# Revit family: Furniture-Workstation-Midmark-Care_Exchange-6281-Wall1
name_source: partatom
category: Furniture
revit_build: Autodesk Revit 2016 (Build: 20170117_1200(x64)
units: mm (PartAtom-declared; Revit-internal decimal feet)

## family parameters
Cut with Voids When Loaded = No
Host = Face
OmniClass Number = 23.40.70.11.14.11
OmniClass Title = Medical Equipment
Room Calculation Point = No
Shared = No

## types (2) — shared parameters
Assembly Code = E1020810
Default Elevation = 4' - 0"
Description = Laptop Wall Mounted Workstation
Manufacturer = Midmark
Material = Paint-Midmark-Mist
Model = 6281
Product Documentation Link = http://my.midmark.com
Product Name = MIDMARK 6281-CARE EXCHANGE® WORKSTATION
Product Page URL = http://www.midmark.com
Type Comments = This wall mounted workstation is designed with independent height adjustment for laptop and tablet based technology components.
URL = www.midmark.com

## per-type parameters (varying)
| type | Platform Depth From Wall | Platform Height From Center | Platform Width From Center | Show Extension Arm | Show Standard Arm |
| 6281 | 2' - 0 1/4" | 0' - 11 1/16" | 0' - 0" | No | Yes |
| 6281 - Extension Arm | 2' - 8" | 0' - 7 1/16" | 0' - 1 1/8" | Yes | No |

## geometry (parser evidence)
native form markers: Blend x2, Sweep x19
no freeform markers — native parametric forms only
